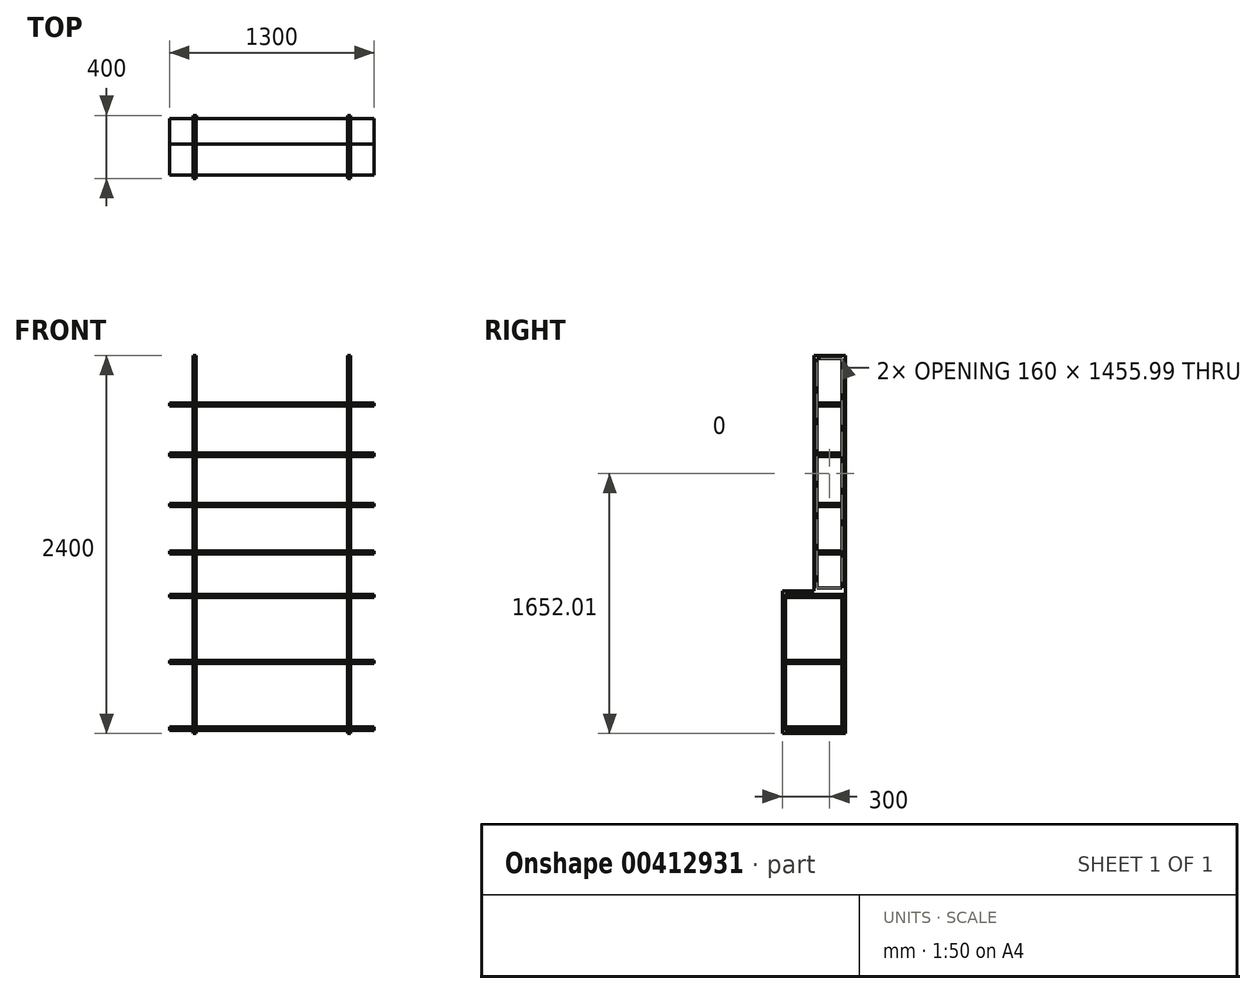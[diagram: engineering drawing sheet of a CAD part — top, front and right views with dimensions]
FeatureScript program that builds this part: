
annotation { "Feature Type Name" : "Feature", "Feature Type Description" : "" }
export const myFeature = defineFeature(function(context is Context, id is Id, definition is map)
    precondition{}
    {
        {
            var Q0;
            Q0=qCreatedBy(makeId("Right.planeOp"),FACE);
            var sketch = newSketch(context, id + "F0", { "sketchPlane" : qUnion([Q0])});
            skLineSegment(sketch, "E0.bottom", {"start": v(200, 1200) * mm, "end": v(-200, 1200) * mm, "construction": true});
            skLineSegment(sketch, "E0.top", {"start": v(200, -1200) * mm, "end": v(-200, -1200) * mm});
            skLineSegment(sketch, "E0.left", {"start": v(200, 1200) * mm, "end": v(200, -1200) * mm});
            skLineSegment(sketch, "E0.right", {"start": v(-200, 1200) * mm, "end": v(-200, -1200) * mm, "construction": true});
            skPoint(sketch, "E0.middle", {"position": v(0, 0) * mm});
            skLineSegment(sketch, "E1.bottom", {"start": v(200, 1200) * mm, "end": v(0, 1200) * mm});
            skLineSegment(sketch, "E1.top", {"start": v(200, -296) * mm, "end": v(0, -296) * mm});
            skLineSegment(sketch, "E1.left", {"start": v(200, 1200) * mm, "end": v(200, -296) * mm});
            skLineSegment(sketch, "E1.right", {"start": v(0, 1200) * mm, "end": v(0, -296) * mm});
            skLineSegment(sketch, "E2.bottom", {"start": v(200, -296) * mm, "end": v(-200, -296) * mm});
            skLineSegment(sketch, "E2.left", {"start": v(200, -296) * mm, "end": v(200, -1200) * mm});
            skLineSegment(sketch, "E2.right", {"start": v(-200, -296) * mm, "end": v(-200, -1200) * mm});
            skSolve(sketch);
        }
        {
            var Q0;
            Q0=makeQuery(id+"F0.imprint","IMPRINT",FACE,{"disambiguationData":[TD([[makeQuery(id+"F0.imprint","IMPRINT",EDGE,{"derivedFrom":sQuery(id+"F0.wireOp",EDGE,"E0.top")}),-1.0]])]});
            var Q1;
            Q1=makeQuery(id+"F0.imprint","IMPRINT",FACE,{"disambiguationData":[TD([[makeQuery(id+"F0.imprint","IMPRINT",EDGE,{"derivedFrom":sQuery(id+"F0.wireOp",EDGE,"E1.bottom")}),1.0]])]});
            extrude(context, id + "F1", {"entities" : qUnion([Q0, Q1]), "depth" : 1300 * mm});
        }
        {
            var Q0;
            Q0=makeQuery(id+"F1.opExtrude","SWEPT_FACE",FACE,{"disambiguationData":[OSD([sQuery(id+"F0.wireOp",EDGE,"E1.right")])]});
            var sketch = newSketch(context, id + "F2", { "sketchPlane" : qUnion([Q0])});
            skLineSegment(sketch, "E3.bottom", {"start": v(0, 1200) * mm, "end": v(150, 1200) * mm});
            skLineSegment(sketch, "E3.top", {"start": v(0, 900) * mm, "end": v(150, 900) * mm});
            skLineSegment(sketch, "E3.left", {"start": v(0, 1200) * mm, "end": v(0, 900) * mm});
            skLineSegment(sketch, "E3.right", {"start": v(150, 1200) * mm, "end": v(150, 900) * mm});
            skLineSegment(sketch, "E4.bottom", {"start": v(170, 1200) * mm, "end": v(1130, 1200) * mm});
            skLineSegment(sketch, "E4.top", {"start": v(170, 900) * mm, "end": v(1130, 900) * mm});
            skLineSegment(sketch, "E4.left", {"start": v(170, 1200) * mm, "end": v(170, 900) * mm});
            skLineSegment(sketch, "E4.right", {"start": v(1130, 1200) * mm, "end": v(1130, 900) * mm});
            skLineSegment(sketch, "E5.bottom", {"start": v(1150, 1200) * mm, "end": v(1300, 1200) * mm});
            skLineSegment(sketch, "E5.top", {"start": v(1150, 900) * mm, "end": v(1300, 900) * mm});
            skLineSegment(sketch, "E5.left", {"start": v(1150, 1200) * mm, "end": v(1150, 900) * mm});
            skLineSegment(sketch, "E5.right", {"start": v(1300, 1200) * mm, "end": v(1300, 900) * mm});
            skLineSegment(sketch, "E6.0.1.0", {"start": v(0, 580) * mm, "end": v(150, 580) * mm});
            skLineSegment(sketch, "E6.0.1.1", {"start": v(150, 880) * mm, "end": v(150, 580) * mm});
            skLineSegment(sketch, "E6.0.1.2", {"start": v(0, 880) * mm, "end": v(0, 580) * mm});
            skLineSegment(sketch, "E6.0.1.3", {"start": v(0, 880) * mm, "end": v(150, 880) * mm});
            skLineSegment(sketch, "E6.0.1.4", {"start": v(170, 880) * mm, "end": v(1130, 880) * mm});
            skLineSegment(sketch, "E6.0.1.5", {"start": v(170, 880) * mm, "end": v(170, 580) * mm});
            skLineSegment(sketch, "E6.0.1.6", {"start": v(170, 580) * mm, "end": v(1130, 580) * mm});
            skLineSegment(sketch, "E6.0.1.7", {"start": v(1150, 880) * mm, "end": v(1300, 880) * mm});
            skLineSegment(sketch, "E6.0.1.8", {"start": v(1130, 880) * mm, "end": v(1130, 580) * mm});
            skLineSegment(sketch, "E6.0.1.9", {"start": v(1150, 880) * mm, "end": v(1150, 580) * mm});
            skLineSegment(sketch, "E6.0.1.10", {"start": v(1300, 880) * mm, "end": v(1300, 580) * mm});
            skLineSegment(sketch, "E6.0.1.11", {"start": v(1150, 580) * mm, "end": v(1300, 580) * mm});
            skLineSegment(sketch, "E6.0.2.0", {"start": v(0, 260) * mm, "end": v(150, 260) * mm});
            skLineSegment(sketch, "E6.0.2.1", {"start": v(150, 560) * mm, "end": v(150, 260) * mm});
            skLineSegment(sketch, "E6.0.2.2", {"start": v(0, 560) * mm, "end": v(0, 260) * mm});
            skLineSegment(sketch, "E6.0.2.3", {"start": v(0, 560) * mm, "end": v(150, 560) * mm});
            skLineSegment(sketch, "E6.0.2.4", {"start": v(170, 560) * mm, "end": v(1130, 560) * mm});
            skLineSegment(sketch, "E6.0.2.5", {"start": v(170, 560) * mm, "end": v(170, 260) * mm});
            skLineSegment(sketch, "E6.0.2.6", {"start": v(170, 260) * mm, "end": v(1130, 260) * mm});
            skLineSegment(sketch, "E6.0.2.7", {"start": v(1150, 560) * mm, "end": v(1300, 560) * mm});
            skLineSegment(sketch, "E6.0.2.8", {"start": v(1130, 560) * mm, "end": v(1130, 260) * mm});
            skLineSegment(sketch, "E6.0.2.9", {"start": v(1150, 560) * mm, "end": v(1150, 260) * mm});
            skLineSegment(sketch, "E6.0.2.10", {"start": v(1300, 560) * mm, "end": v(1300, 260) * mm});
            skLineSegment(sketch, "E6.0.2.11", {"start": v(1150, 260) * mm, "end": v(1300, 260) * mm});
            skLineSegment(sketch, "E6.0.3.1", {"start": v(150, 240) * mm, "end": v(150, -40) * mm});
            skLineSegment(sketch, "E6.0.3.2", {"start": v(0, 240) * mm, "end": v(0, -40) * mm});
            skLineSegment(sketch, "E6.0.3.3", {"start": v(0, 240) * mm, "end": v(150, 240) * mm});
            skLineSegment(sketch, "E6.0.3.4", {"start": v(170, 240) * mm, "end": v(1130, 240) * mm});
            skLineSegment(sketch, "E6.0.3.5", {"start": v(170, 240) * mm, "end": v(170, -40) * mm});
            skLineSegment(sketch, "E6.0.3.7", {"start": v(1150, 240) * mm, "end": v(1300, 240) * mm});
            skLineSegment(sketch, "E6.0.3.8", {"start": v(1130, 240) * mm, "end": v(1130, -40) * mm});
            skLineSegment(sketch, "E6.0.3.9", {"start": v(1150, 240) * mm, "end": v(1150, -40) * mm});
            skLineSegment(sketch, "E6.0.3.10", {"start": v(1300, 240) * mm, "end": v(1300, -40) * mm});
            skLineSegment(sketch, "E6.direction1", {"start": v(0, 900) * mm, "end": v(25.4, 900) * mm, "construction": true});
            skLineSegment(sketch, "E6.direction2", {"start": v(0, 900) * mm, "end": v(0, 580) * mm, "construction": true});
            skLineSegment(sketch, "E7", {"start": v(0, -60) * mm, "end": v(0, -296) * mm});
            skLineSegment(sketch, "E8", {"start": v(0, -296) * mm, "end": v(150, -296) * mm});
            skLineSegment(sketch, "E9", {"start": v(150, -296) * mm, "end": v(150, -60) * mm});
            skLineSegment(sketch, "E10", {"start": v(170, -60) * mm, "end": v(170, -296) * mm});
            skLineSegment(sketch, "E11", {"start": v(170, -296) * mm, "end": v(1130, -296) * mm});
            skLineSegment(sketch, "E12", {"start": v(1130, -296) * mm, "end": v(1130, -60) * mm});
            skLineSegment(sketch, "E13", {"start": v(1150, -60) * mm, "end": v(1150, -296) * mm});
            skLineSegment(sketch, "E14", {"start": v(1150, -296) * mm, "end": v(1300, -296) * mm});
            skLineSegment(sketch, "E15", {"start": v(1300, -296) * mm, "end": v(1300, -60) * mm});
            skLineSegment(sketch, "E16.bottom", {"start": v(0, -60) * mm, "end": v(150, -60) * mm});
            skLineSegment(sketch, "E16.top", {"start": v(0, -40) * mm, "end": v(150, -40) * mm});
            skLineSegment(sketch, "E17.bottom", {"start": v(170, -60) * mm, "end": v(1130, -60) * mm});
            skLineSegment(sketch, "E17.top", {"start": v(170, -40) * mm, "end": v(1130, -40) * mm});
            skLineSegment(sketch, "E18.bottom", {"start": v(1150, -60) * mm, "end": v(1300, -60) * mm});
            skLineSegment(sketch, "E18.top", {"start": v(1150, -40) * mm, "end": v(1300, -40) * mm});
            skSolve(sketch);
        }
        {
            var Q0;
            Q0 = qSketchRegion(id + "F2", true);
            extrude(context, id + "F3", {"entities" : qUnion([Q0]), "operationType" : NewBodyOperationType.REMOVE, "endBound" : BoundingType.UP_TO_NEXT, "oppositeDirection" : true, "depth" : 25.4 * mm});
        }
        {
            var Q0;
            Q0=makeQuery(id+"F3.boolean.opBoolean","COPY",FACE,{"derivedFrom":makeQuery(id+"F3.opExtrude","SWEPT_FACE",FACE,{"disambiguationData":[OSD([sQuery(id+"F2.wireOp",EDGE,"E3.right")])]})});
            var sketch = newSketch(context, id + "F4", { "sketchPlane" : qUnion([Q0])});
            skLineSegment(sketch, "E19.bottom", {"start": v(-180, 1180) * mm, "end": v(-20, 1180) * mm});
            skLineSegment(sketch, "E19.top", {"start": v(-180, 900) * mm, "end": v(-20, 900) * mm});
            skLineSegment(sketch, "E19.left", {"start": v(-180, 1180) * mm, "end": v(-180, 900) * mm});
            skLineSegment(sketch, "E19.right", {"start": v(-20, 1180) * mm, "end": v(-20, 900) * mm});
            skLineSegment(sketch, "E20.bottom", {"start": v(-180, 880) * mm, "end": v(-20, 880) * mm});
            skLineSegment(sketch, "E20.top", {"start": v(-180, 580) * mm, "end": v(-20, 580) * mm});
            skLineSegment(sketch, "E20.left", {"start": v(-180, 880) * mm, "end": v(-180, 580) * mm});
            skLineSegment(sketch, "E20.right", {"start": v(-20, 880) * mm, "end": v(-20, 580) * mm});
            skLineSegment(sketch, "E21.bottom", {"start": v(-180, 560) * mm, "end": v(-20, 560) * mm});
            skLineSegment(sketch, "E21.top", {"start": v(-180, 260) * mm, "end": v(-20, 260) * mm});
            skLineSegment(sketch, "E21.left", {"start": v(-180, 560) * mm, "end": v(-180, 260) * mm});
            skLineSegment(sketch, "E21.right", {"start": v(-20, 560) * mm, "end": v(-20, 260) * mm});
            skLineSegment(sketch, "E22.bottom", {"start": v(-180, 240) * mm, "end": v(-20, 240) * mm});
            skLineSegment(sketch, "E22.top", {"start": v(-180, -276) * mm, "end": v(-20, -276) * mm});
            skLineSegment(sketch, "E22.left", {"start": v(-180, 240) * mm, "end": v(-180, -40) * mm});
            skLineSegment(sketch, "E22.right", {"start": v(-20, 240) * mm, "end": v(-20, -40) * mm});
            skLineSegment(sketch, "E23.bottom", {"start": v(-180, -40) * mm, "end": v(-20, -40) * mm});
            skLineSegment(sketch, "E23.top", {"start": v(-180, -60) * mm, "end": v(-20, -60) * mm});
            skLineSegment(sketch, "E24.trimOffspring", {"start": v(-20, -60) * mm, "end": v(-20, -276) * mm});
            skLineSegment(sketch, "E25.trimOffspring", {"start": v(-180, -60) * mm, "end": v(-180, -276) * mm});
            skSolve(sketch);
        }
        {
            var Q0;
            Q0 = qSketchRegion(id + "F4", true);
            extrude(context, id + "F5", {"entities" : qUnion([Q0]), "operationType" : NewBodyOperationType.REMOVE, "endBound" : BoundingType.THROUGH_ALL, "oppositeDirection" : true, "depth" : 25.4 * mm});
        }
        {
            var Q0;
            Q0=makeQuery(id+"F5.boolean.opBoolean","MERGE",FACE,{"derivedFrom":[makeQuery(id+"F3.boolean.opBoolean","COPY",FACE,{"derivedFrom":makeQuery(id+"F3.opExtrude","SWEPT_FACE",FACE,{"disambiguationData":[OSD([sQuery(id+"F2.wireOp",EDGE,"E3.top")])]})}),makeQuery(id+"F3.boolean.opBoolean","COPY",FACE,{"derivedFrom":makeQuery(id+"F3.opExtrude","SWEPT_FACE",FACE,{"disambiguationData":[OSD([sQuery(id+"F2.wireOp",EDGE,"E4.top")])]})}),makeQuery(id+"F3.boolean.opBoolean","COPY",FACE,{"derivedFrom":makeQuery(id+"F3.opExtrude","SWEPT_FACE",FACE,{"disambiguationData":[OSD([sQuery(id+"F2.wireOp",EDGE,"E5.top")])]})}),makeQuery(id+"F5.opExtrude","SWEPT_FACE",FACE,{"disambiguationData":[OSD([sQuery(id+"F4.wireOp",EDGE,"E19.top")])]})]});
            var sketch = newSketch(context, id + "F6", { "sketchPlane" : qUnion([Q0])});
            skLineSegment(sketch, "E26.bottom", {"start": v(0, 200) * mm, "end": v(150, 200) * mm});
            skLineSegment(sketch, "E26.top", {"start": v(0, 180) * mm, "end": v(150, 180) * mm});
            skLineSegment(sketch, "E26.left", {"start": v(0, 200) * mm, "end": v(0, 180) * mm});
            skLineSegment(sketch, "E26.right", {"start": v(150, 200) * mm, "end": v(150, 180) * mm});
            skLineSegment(sketch, "E27.bottom", {"start": v(0, 0) * mm, "end": v(150, 0) * mm});
            skLineSegment(sketch, "E27.top", {"start": v(0, 20) * mm, "end": v(150, 20) * mm});
            skLineSegment(sketch, "E27.left", {"start": v(0, 0) * mm, "end": v(0, 20) * mm});
            skLineSegment(sketch, "E27.right", {"start": v(150, 0) * mm, "end": v(150, 20) * mm});
            skLineSegment(sketch, "E28.bottom", {"start": v(1300, 200) * mm, "end": v(1150, 200) * mm});
            skLineSegment(sketch, "E28.top", {"start": v(1300, 180) * mm, "end": v(1150, 180) * mm});
            skLineSegment(sketch, "E28.left", {"start": v(1300, 200) * mm, "end": v(1300, 180) * mm});
            skLineSegment(sketch, "E28.right", {"start": v(1150, 200) * mm, "end": v(1150, 180) * mm});
            skLineSegment(sketch, "E29.bottom", {"start": v(1300, 0) * mm, "end": v(1150, 0) * mm});
            skLineSegment(sketch, "E29.top", {"start": v(1300, 20) * mm, "end": v(1150, 20) * mm});
            skLineSegment(sketch, "E29.left", {"start": v(1300, 0) * mm, "end": v(1300, 20) * mm});
            skLineSegment(sketch, "E29.right", {"start": v(1150, 0) * mm, "end": v(1150, 20) * mm});
            skLineSegment(sketch, "E30.bottom", {"start": v(170, 200) * mm, "end": v(1130, 200) * mm});
            skLineSegment(sketch, "E30.top", {"start": v(170, 180) * mm, "end": v(1130, 180) * mm});
            skLineSegment(sketch, "E30.left", {"start": v(170, 200) * mm, "end": v(170, 180) * mm});
            skLineSegment(sketch, "E30.right", {"start": v(1130, 200) * mm, "end": v(1130, 180) * mm});
            skLineSegment(sketch, "E31.bottom", {"start": v(170, 0) * mm, "end": v(1130, 0) * mm});
            skLineSegment(sketch, "E31.top", {"start": v(170, 20) * mm, "end": v(1130, 20) * mm});
            skLineSegment(sketch, "E31.left", {"start": v(170, 0) * mm, "end": v(170, 20) * mm});
            skLineSegment(sketch, "E31.right", {"start": v(1130, 0) * mm, "end": v(1130, 20) * mm});
            skSolve(sketch);
        }
        {
            var Q0;
            Q0 = qSketchRegion(id + "F6", true);
            var Q1;
            Q1=makeQuery(id+"F3.boolean.opBoolean","MERGE",FACE,{"derivedFrom":[makeQuery(id+"F1.opExtrude","SWEPT_FACE",FACE,{"disambiguationData":[OSD([sQuery(id+"F0.wireOp",EDGE,"E2.bottom")])]}),makeQuery(id+"F3.opExtrude","SWEPT_FACE",FACE,{"disambiguationData":[OSD([sQuery(id+"F2.wireOp",EDGE,"E8")])]}),makeQuery(id+"F3.opExtrude","SWEPT_FACE",FACE,{"disambiguationData":[OSD([sQuery(id+"F2.wireOp",EDGE,"E11")])]}),makeQuery(id+"F3.opExtrude","SWEPT_FACE",FACE,{"disambiguationData":[OSD([sQuery(id+"F2.wireOp",EDGE,"E14")])]})]});
            extrude(context, id + "F7", {"entities" : qUnion([Q0]), "operationType" : NewBodyOperationType.REMOVE, "endBound" : BoundingType.UP_TO_SURFACE, "oppositeDirection" : true, "endBoundEntityFace" : qUnion([Q1]), "depth" : 25.4 * mm});
        }
        {
            var Q0;
            Q0=makeQuery(id+"F1.opExtrude","SWEPT_FACE",FACE,{"disambiguationData":[OSD([sQuery(id+"F0.wireOp",EDGE,"E2.right")])]});
            var sketch = newSketch(context, id + "F8", { "sketchPlane" : qUnion([Q0])});
            skLineSegment(sketch, "E32.bottom", {"start": v(1300, -1160) * mm, "end": v(1150, -1160) * mm});
            skLineSegment(sketch, "E32.top", {"start": v(1300, -756) * mm, "end": v(1150, -756) * mm});
            skLineSegment(sketch, "E32.left", {"start": v(1300, -1160) * mm, "end": v(1300, -756) * mm});
            skLineSegment(sketch, "E32.right", {"start": v(1150, -1160) * mm, "end": v(1150, -756) * mm});
            skLineSegment(sketch, "E33.bottom", {"start": v(1300, -336) * mm, "end": v(1150, -336) * mm});
            skLineSegment(sketch, "E33.top", {"start": v(1300, -736) * mm, "end": v(1150, -736) * mm});
            skLineSegment(sketch, "E33.left", {"start": v(1300, -336) * mm, "end": v(1300, -736) * mm});
            skLineSegment(sketch, "E33.right", {"start": v(1150, -336) * mm, "end": v(1150, -736) * mm});
            skLineSegment(sketch, "E34.bottom", {"start": v(1130, -336) * mm, "end": v(170, -336) * mm});
            skLineSegment(sketch, "E34.top", {"start": v(1130, -736) * mm, "end": v(170, -736) * mm});
            skLineSegment(sketch, "E34.left", {"start": v(1130, -336) * mm, "end": v(1130, -736) * mm});
            skLineSegment(sketch, "E34.right", {"start": v(170, -336) * mm, "end": v(170, -736) * mm});
            skLineSegment(sketch, "E35.bottom", {"start": v(170, -756) * mm, "end": v(1130, -756) * mm});
            skLineSegment(sketch, "E35.top", {"start": v(170, -1160) * mm, "end": v(1130, -1160) * mm});
            skLineSegment(sketch, "E35.left", {"start": v(170, -756) * mm, "end": v(170, -1160) * mm});
            skLineSegment(sketch, "E35.right", {"start": v(1130, -756) * mm, "end": v(1130, -1160) * mm});
            skLineSegment(sketch, "E36.bottom", {"start": v(0, -336) * mm, "end": v(150, -336) * mm});
            skLineSegment(sketch, "E36.top", {"start": v(0, -736) * mm, "end": v(150, -736) * mm});
            skLineSegment(sketch, "E36.left", {"start": v(0, -336) * mm, "end": v(0, -736) * mm});
            skLineSegment(sketch, "E36.right", {"start": v(150, -336) * mm, "end": v(150, -736) * mm});
            skLineSegment(sketch, "E37.bottom", {"start": v(0, -1160) * mm, "end": v(150, -1160) * mm});
            skLineSegment(sketch, "E37.top", {"start": v(0, -756) * mm, "end": v(150, -756) * mm});
            skLineSegment(sketch, "E37.left", {"start": v(0, -1160) * mm, "end": v(0, -756) * mm});
            skLineSegment(sketch, "E37.right", {"start": v(150, -1160) * mm, "end": v(150, -756) * mm});
            skLineSegment(sketch, "E38.bottom", {"start": v(0, -296) * mm, "end": v(150, -296) * mm});
            skLineSegment(sketch, "E38.top", {"start": v(0, -316) * mm, "end": v(150, -316) * mm});
            skLineSegment(sketch, "E38.left", {"start": v(0, -296) * mm, "end": v(0, -316) * mm});
            skLineSegment(sketch, "E38.right", {"start": v(150, -296) * mm, "end": v(150, -316) * mm});
            skLineSegment(sketch, "E39.bottom", {"start": v(170, -296) * mm, "end": v(1130, -296) * mm});
            skLineSegment(sketch, "E39.top", {"start": v(170, -316) * mm, "end": v(1130, -316) * mm});
            skLineSegment(sketch, "E39.left", {"start": v(170, -296) * mm, "end": v(170, -316) * mm});
            skLineSegment(sketch, "E39.right", {"start": v(1130, -296) * mm, "end": v(1130, -316) * mm});
            skLineSegment(sketch, "E40.bottom", {"start": v(1300, -296) * mm, "end": v(1150, -296) * mm});
            skLineSegment(sketch, "E40.top", {"start": v(1300, -316) * mm, "end": v(1150, -316) * mm});
            skLineSegment(sketch, "E40.left", {"start": v(1300, -296) * mm, "end": v(1300, -316) * mm});
            skLineSegment(sketch, "E40.right", {"start": v(1150, -296) * mm, "end": v(1150, -316) * mm});
            skLineSegment(sketch, "E41.bottom", {"start": v(0, -1200) * mm, "end": v(150, -1200) * mm});
            skLineSegment(sketch, "E41.top", {"start": v(0, -1180) * mm, "end": v(150, -1180) * mm});
            skLineSegment(sketch, "E41.left", {"start": v(0, -1200) * mm, "end": v(0, -1180) * mm});
            skLineSegment(sketch, "E41.right", {"start": v(150, -1200) * mm, "end": v(150, -1180) * mm});
            skLineSegment(sketch, "E42.bottom", {"start": v(170, -1200) * mm, "end": v(1130, -1200) * mm});
            skLineSegment(sketch, "E42.top", {"start": v(170, -1180) * mm, "end": v(1130, -1180) * mm});
            skLineSegment(sketch, "E42.left", {"start": v(170, -1200) * mm, "end": v(170, -1180) * mm});
            skLineSegment(sketch, "E42.right", {"start": v(1130, -1200) * mm, "end": v(1130, -1180) * mm});
            skLineSegment(sketch, "E43.bottom", {"start": v(1300, -1200) * mm, "end": v(1150, -1200) * mm});
            skLineSegment(sketch, "E43.top", {"start": v(1300, -1180) * mm, "end": v(1150, -1180) * mm});
            skLineSegment(sketch, "E43.left", {"start": v(1300, -1200) * mm, "end": v(1300, -1180) * mm});
            skLineSegment(sketch, "E43.right", {"start": v(1150, -1200) * mm, "end": v(1150, -1180) * mm});
            skSolve(sketch);
        }
        {
            var Q0;
            Q0 = qSketchRegion(id + "F8", true);
            extrude(context, id + "F9", {"entities" : qUnion([Q0]), "operationType" : NewBodyOperationType.REMOVE, "endBound" : BoundingType.THROUGH_ALL, "oppositeDirection" : true, "depth" : 25.4 * mm});
        }
        {
            var Q0;
            {var subQ1=makeQuery(id+"F1.opExtrude","SWEPT_FACE",FACE,{"disambiguationData":[OSD([sQuery(id+"F0.wireOp",EDGE,"E1.right")])]});var subQ9=makeQuery(id+"F3.boolean.opBoolean","COPY",FACE,{"derivedFrom":makeQuery(id+"F3.opExtrude","SWEPT_FACE",FACE,{"disambiguationData":[OSD([sQuery(id+"F2.wireOp",EDGE,"E6.0.3.1")])]})});var subQ19=makeQuery(id+"F3.boolean.opBoolean","COPY",FACE,{"derivedFrom":makeQuery(id+"F3.opExtrude","SWEPT_FACE",FACE,{"disambiguationData":[OSD([sQuery(id+"F2.wireOp",EDGE,"E6.0.2.1")])]})});var subQ28=makeQuery(id+"F3.boolean.opBoolean","COPY",FACE,{"derivedFrom":makeQuery(id+"F3.opExtrude","SWEPT_FACE",FACE,{"disambiguationData":[OSD([sQuery(id+"F2.wireOp",EDGE,"E6.0.1.1")])]})});Q0=makeQuery(id+"F9.boolean.opBoolean","MERGE",FACE,{"derivedFrom":[makeQuery(id+"F7.boolean.opBoolean","MERGE",FACE,{"derivedFrom":[makeQuery(id+"F3.boolean.opBoolean","COPY",FACE,{"derivedFrom":makeQuery(id+"F3.opExtrude","SWEPT_FACE",FACE,{"disambiguationData":[OSD([sQuery(id+"F2.wireOp",EDGE,"E3.right")])]})}),makeQuery(id+"F3.boolean.opBoolean","COPY",FACE,{"derivedFrom":makeQuery(id+"F3.opExtrude","SWEPT_FACE",FACE,{"disambiguationData":[OSD([sQuery(id+"F2.wireOp",EDGE,"E9")])]})}),makeQuery(id+"F5.boolean.opBoolean","SPLIT",FACE,{"disambiguationData":[TD([makeQuery(id+"F5.opExtrude","SWEPT_FACE",FACE,{"disambiguationData":[OSD([sQuery(id+"F4.wireOp",EDGE,"E20.left")])]})])],"derivedFrom":subQ28}),makeQuery(id+"F5.boolean.opBoolean","SPLIT",FACE,{"disambiguationData":[TD([subQ1])],"derivedFrom":subQ28}),makeQuery(id+"F5.boolean.opBoolean","SPLIT",FACE,{"disambiguationData":[TD([makeQuery(id+"F5.opExtrude","SWEPT_FACE",FACE,{"disambiguationData":[OSD([sQuery(id+"F4.wireOp",EDGE,"E21.left")])]})])],"derivedFrom":subQ19}),makeQuery(id+"F5.boolean.opBoolean","SPLIT",FACE,{"disambiguationData":[TD([subQ1])],"derivedFrom":subQ19}),makeQuery(id+"F5.boolean.opBoolean","SPLIT",FACE,{"disambiguationData":[TD([makeQuery(id+"F5.opExtrude","SWEPT_FACE",FACE,{"disambiguationData":[OSD([sQuery(id+"F4.wireOp",EDGE,"E22.left")])]})])],"derivedFrom":subQ9}),makeQuery(id+"F5.boolean.opBoolean","SPLIT",FACE,{"disambiguationData":[TD([subQ1])],"derivedFrom":subQ9}),makeQuery(id+"F7.opExtrude","SWEPT_FACE",FACE,{"disambiguationData":[OSD([sQuery(id+"F6.wireOp",EDGE,"E26.right")])]}),makeQuery(id+"F7.opExtrude","SWEPT_FACE",FACE,{"disambiguationData":[OSD([sQuery(id+"F6.wireOp",EDGE,"E27.right")])]})]}),makeQuery(id+"F9.opExtrude","SWEPT_FACE",FACE,{"disambiguationData":[OSD([sQuery(id+"F8.wireOp",EDGE,"eA5yIezF-Y2pl-mjIO-ghK7-0rxZHP1I57Hn.right")])]})]});}
            var sketch = newSketch(context, id + "F10", { "sketchPlane" : qUnion([Q0])});
            skLineSegment(sketch, "E44.bottom", {"start": v(180, -736) * mm, "end": v(-180, -736) * mm});
            skLineSegment(sketch, "E44.top", {"start": v(180, -336) * mm, "end": v(-180, -336) * mm});
            skLineSegment(sketch, "E44.left", {"start": v(180, -736) * mm, "end": v(180, -336) * mm});
            skLineSegment(sketch, "E44.right", {"start": v(-180, -736) * mm, "end": v(-180, -336) * mm});
            skLineSegment(sketch, "E45.bottom", {"start": v(-180, -756) * mm, "end": v(180, -756) * mm});
            skLineSegment(sketch, "E45.top", {"start": v(-180, -1160) * mm, "end": v(180, -1160) * mm});
            skLineSegment(sketch, "E45.left", {"start": v(-180, -756) * mm, "end": v(-180, -1160) * mm});
            skLineSegment(sketch, "E45.right", {"start": v(180, -756) * mm, "end": v(180, -1160) * mm});
            skPoint(sketch, "E46.top.end.orphan", {"position": v(180, -907.66) * mm});
            skSolve(sketch);
        }
        {
            var Q0;
            Q0 = qSketchRegion(id + "F10", true);
            extrude(context, id + "F11", {"entities" : qUnion([Q0]), "operationType" : NewBodyOperationType.REMOVE, "endBound" : BoundingType.THROUGH_ALL, "oppositeDirection" : true, "depth" : 25.4 * mm});
        }
        {
            var Q0;
            Q0=makeQuery(id+"F9.boolean.opBoolean","COPY",FACE,{"derivedFrom":makeQuery(id+"F9.opExtrude","SWEPT_FACE",FACE,{"disambiguationData":[OSD([sQuery(id+"F8.wireOp",EDGE,"E38.top")])]})});
            var sketch = newSketch(context, id + "F12", { "sketchPlane" : qUnion([Q0])});
            skLineSegment(sketch, "E47.bottom", {"start": v(0, 200) * mm, "end": v(150, 200) * mm});
            skLineSegment(sketch, "E47.top", {"start": v(0, 180) * mm, "end": v(150, 180) * mm});
            skLineSegment(sketch, "E47.left", {"start": v(0, 200) * mm, "end": v(0, 180) * mm});
            skLineSegment(sketch, "E47.right", {"start": v(150, 200) * mm, "end": v(150, 180) * mm});
            skLineSegment(sketch, "E48.bottom", {"start": v(0, -200) * mm, "end": v(150, -200) * mm});
            skLineSegment(sketch, "E48.top", {"start": v(0, -180) * mm, "end": v(150, -180) * mm});
            skLineSegment(sketch, "E48.left", {"start": v(0, -200) * mm, "end": v(0, -180) * mm});
            skLineSegment(sketch, "E48.right", {"start": v(150, -200) * mm, "end": v(150, -180) * mm});
            skLineSegment(sketch, "E49.bottom", {"start": v(170.78, 200) * mm, "end": v(1130.1, 200) * mm});
            skLineSegment(sketch, "E49.top", {"start": v(170.78, 180) * mm, "end": v(1130.1, 180) * mm});
            skLineSegment(sketch, "E49.left", {"start": v(170.78, 200) * mm, "end": v(170.78, 180) * mm});
            skLineSegment(sketch, "E49.right", {"start": v(1130.1, 200) * mm, "end": v(1130.1, 180) * mm});
            skLineSegment(sketch, "E50.bottom", {"start": v(1300.1, 200) * mm, "end": v(1150.1, 200) * mm});
            skLineSegment(sketch, "E50.top", {"start": v(1300.1, 180) * mm, "end": v(1150.1, 180) * mm});
            skLineSegment(sketch, "E50.left", {"start": v(1300.1, 200) * mm, "end": v(1300.1, 180) * mm});
            skLineSegment(sketch, "E50.right", {"start": v(1150.1, 200) * mm, "end": v(1150.1, 180) * mm});
            skLineSegment(sketch, "E51.bottom", {"start": v(1300, -200) * mm, "end": v(1150, -200) * mm});
            skLineSegment(sketch, "E51.top", {"start": v(1300, -180) * mm, "end": v(1150, -180) * mm});
            skLineSegment(sketch, "E51.left", {"start": v(1300, -200) * mm, "end": v(1300, -180) * mm});
            skLineSegment(sketch, "E51.right", {"start": v(1150, -200) * mm, "end": v(1150, -180) * mm});
            skLineSegment(sketch, "E52.bottom", {"start": v(169.85, -200) * mm, "end": v(1130.1, -200) * mm});
            skLineSegment(sketch, "E52.top", {"start": v(169.85, -180) * mm, "end": v(1130.1, -180) * mm});
            skLineSegment(sketch, "E52.left", {"start": v(169.85, -200) * mm, "end": v(169.85, -180) * mm});
            skLineSegment(sketch, "E52.right", {"start": v(1130.1, -200) * mm, "end": v(1130.1, -180) * mm});
            skSolve(sketch);
        }
        {
            var Q0;
            Q0 = qSketchRegion(id + "F12", true);
            extrude(context, id + "F13", {"entities" : qUnion([Q0]), "operationType" : NewBodyOperationType.REMOVE, "endBound" : BoundingType.THROUGH_ALL, "oppositeDirection" : true, "depth" : 25.4 * mm});
        }
    });
